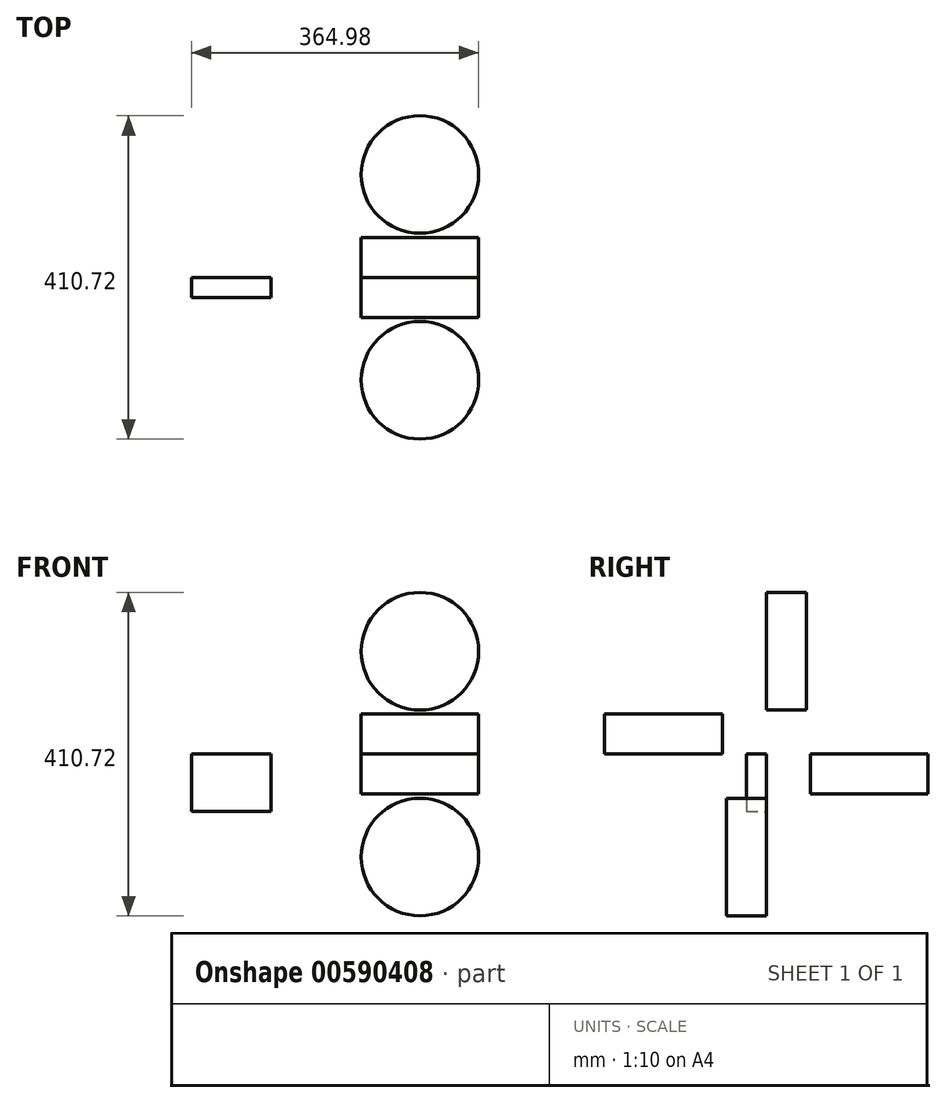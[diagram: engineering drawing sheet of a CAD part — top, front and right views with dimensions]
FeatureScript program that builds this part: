
annotation { "Feature Type Name" : "Feature", "Feature Type Description" : "" }
export const myFeature = defineFeature(function(context is Context, id is Id, definition is map)
    precondition{}
    {
        {
            var Q0;
            Q0=qCreatedBy(makeId("Front.planeOp"),FACE);
            var sketch = newSketch(context, id + "F0", { "sketchPlane" : qUnion([Q0])});
            skLineSegment(sketch, "E0.bottom", {"start": v(-208.28, 70.28) * mm, "end": v(-106.8, 70.28) * mm});
            skLineSegment(sketch, "E0.top", {"start": v(-208.28, -2.74) * mm, "end": v(-106.8, -2.74) * mm});
            skLineSegment(sketch, "E0.left", {"start": v(-208.28, 70.28) * mm, "end": v(-208.28, -2.74) * mm});
            skLineSegment(sketch, "E0.right", {"start": v(-106.8, 70.28) * mm, "end": v(-106.8, -2.74) * mm});
            skCircle(sketch, "E1", {"center": v(82.03, -60.4) * mm, "radius": 74.67 * mm});
            skSolve(sketch);
        }
        {
            var Q0;
            Q0 = qSketchRegion(id + "F0", true);
            extrude(context, id + "F1", {"entities" : qUnion([Q0]), "depth" : 25.4 * mm, "offsetDistance" : 25.4 * mm});
        }
        {
            var Q0;
            Q0=makeQuery(id+"F1.opExtrude","CAP_FACE",FACE,{"disambiguationData":[OSD([sQuery(id+"F0.wireOp",EDGE,"E1")])],"isStart":false});
            extrude(context, id + "F2", {"entities" : qUnion([Q0]), "operationType" : NewBodyOperationType.ADD, "depth" : 25.4 * mm, "offsetDistance" : 25.4 * mm});
        }
        {
            var Q0;
            Q0=makeQuery(id+"F1.opExtrude","SWEPT_BODY",BODY,{"disambiguationData":[OSD([sQuery(id+"F0.wireOp",EDGE,"E1")])]});
            var Q1;
            Q1=makeQuery(id+"F1.opExtrude","CAP_EDGE",EDGE,{"disambiguationData":[OSD([sQuery(id+"F0.wireOp",EDGE,"E0.bottom")])],"isStart":true});
            circularPattern(context, id + "F3", {"entities" : qUnion([Q0]), "axis" : qUnion([Q1]), "angle" : 360 * degree, "instanceCount" : 4, "equalSpace" : true});
        }
    });
